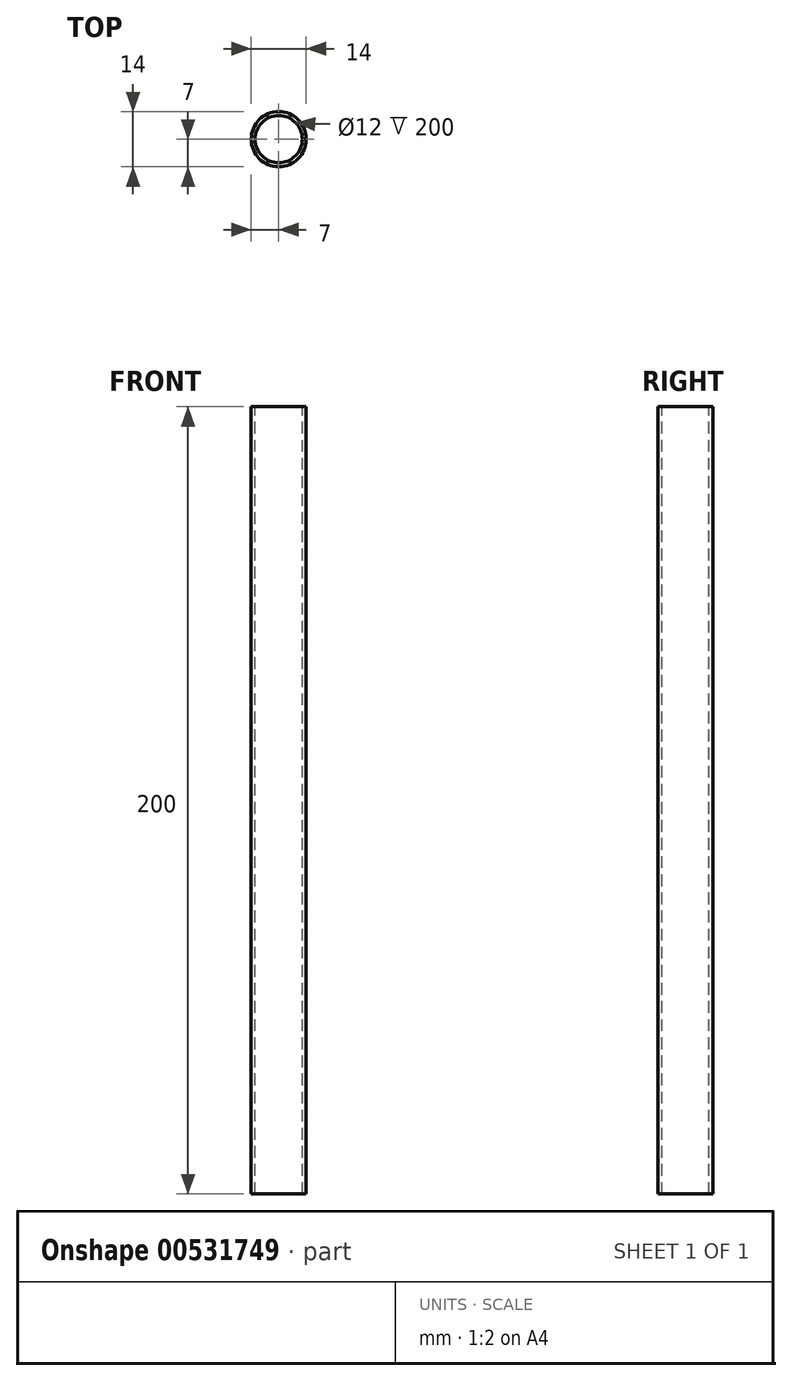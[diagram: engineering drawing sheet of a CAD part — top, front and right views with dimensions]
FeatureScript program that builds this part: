
annotation { "Feature Type Name" : "Feature", "Feature Type Description" : "" }
export const myFeature = defineFeature(function(context is Context, id is Id, definition is map)
    precondition{}
    {
        {
            var Q0;
            Q0=qCreatedBy(makeId("Front.planeOp"),FACE);
            var sketch = newSketch(context, id + "F0", { "sketchPlane" : qUnion([Q0])});
            skLineSegment(sketch, "E0", {"start": v(-6, 33.7) * mm, "end": v(-6, -166.3) * mm});
            skLineSegment(sketch, "E1", {"start": v(-6, -166.3) * mm, "end": v(0, -166.3) * mm});
            skLineSegment(sketch, "E2", {"start": v(0, -166.3) * mm, "end": v(1, -166.3) * mm});
            skLineSegment(sketch, "E3", {"start": v(1, -166.3) * mm, "end": v(1, 33.7) * mm});
            skLineSegment(sketch, "E4", {"start": v(1, 33.7) * mm, "end": v(0, 33.7) * mm});
            skLineSegment(sketch, "E5", {"start": v(0, 33.7) * mm, "end": v(-6, 33.7) * mm});
            skLineSegment(sketch, "E6", {"start": v(0, 33.7) * mm, "end": v(0, -166.3) * mm});
            skSolve(sketch);
        }
        {
            var Q0;
            Q0=makeQuery(id+"F0.imprint","IMPRINT",FACE,{"disambiguationData":[TD([[makeQuery(id+"F0.imprint","IMPRINT",EDGE,{"derivedFrom":sQuery(id+"F0.wireOp",EDGE,"E2")}),1.0]])]});
            var Q1;
            Q1=sQuery(id+"F0.wireOp",EDGE,"E0");
            revolve(context, id + "F1", {"surfaceOperationType" : NewSurfaceOperationType.NEW, "entities" : qUnion([Q0]), "axis" : qUnion([Q1]), "revolveType" : RevolveType.FULL});
        }
    });
